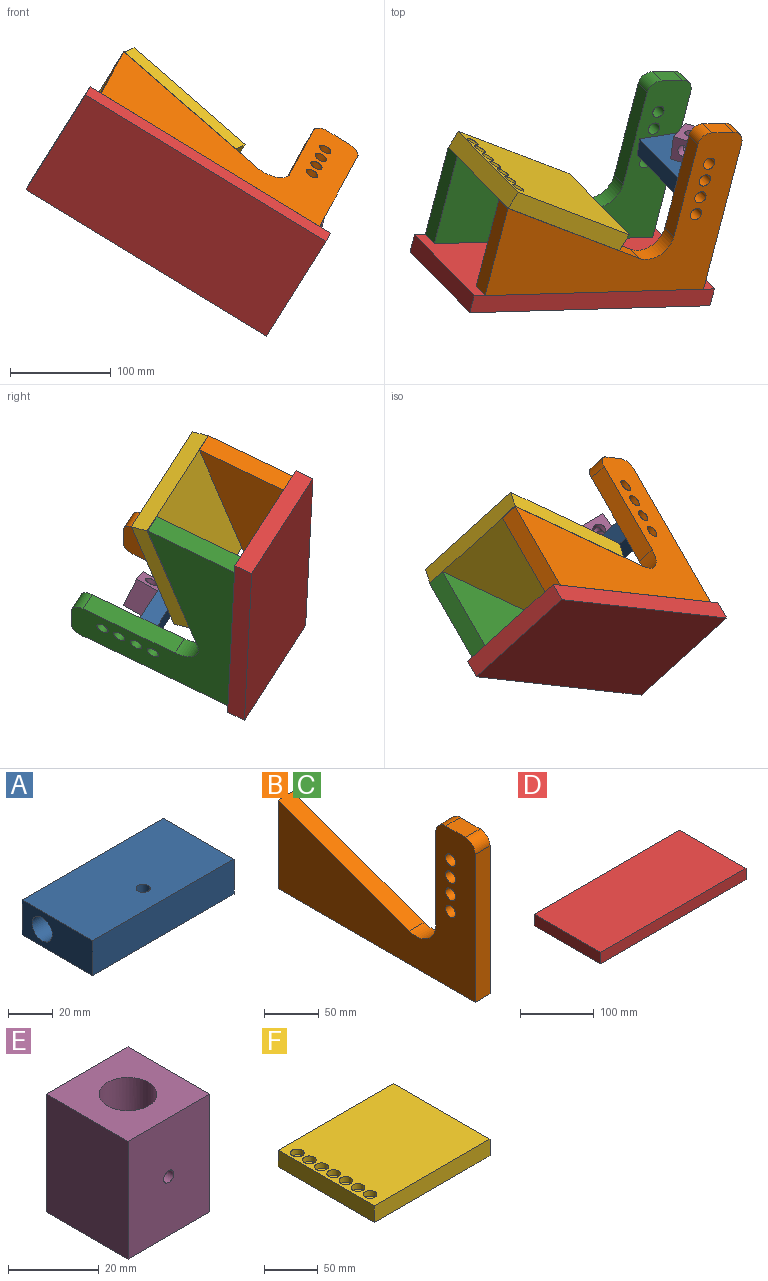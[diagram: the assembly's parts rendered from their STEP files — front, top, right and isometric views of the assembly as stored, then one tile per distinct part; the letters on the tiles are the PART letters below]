
ASSEMBLY  parts=6 mates=5
PART A: 8 faces, bbox 88.9x44.5x19.1 mm
  f0: plane 44.45x19.05mm, normal (-1,0,0), area 720.1mm2, adj f1,f3,f4,f5,f6
  f1: plane 88.9x19.05mm, normal (0,-1,0), area 1693.5mm2, adj f0,f2,f4,f5
  f2: plane 44.45x19.05mm, normal (1,0,0), area 720.1mm2, adj f1,f3,f4,f5,f6
  f3: plane 88.9x19.05mm, normal (0,1,0), area 1693.5mm2, adj f0,f2,f4,f5
  f4: plane 88.9x44.45mm, normal (0,0,1), area 3919.9mm2, adj f0,f1,f2,f3,f7
  f5: plane 88.9x44.45mm, normal (0,0,-1), area 3919.9mm2, adj f0,f1,f2,f3,f7
  f6: cylinder r=6.35mm len=88.9mm, axis (-1,0,0), area 3547mm2, adj f0,f2
  f7: cylinder r=3.17mm len=19.05mm, axis (0,0,1), area 380mm2, adj f4,f5
PART B: 15 faces, bbox 19.1x254x177.8 mm
  f0: plane 25.4x19.05mm, normal (0,0,1), area 483.9mm2, adj f1,f12,f13,f14
  f1: cylinder r=12.7mm len=19.05mm, axis (-1,0,0), area 380mm2, adj f0,f2,f13,f14
  f2: plane 165.1x19.05mm, normal (0,-1,0), area 3145.2mm2, adj f1,f3,f13,f14
  f3: plane 254x19.05mm, normal (0,0,-1), area 4838.7mm2, adj f2,f4,f13,f14
  f4: plane 98.8x19.05mm, normal (0,1,0), area 1882.1mm2, adj f3,f5,f13,f14
  f5: plane 169.11x61.55mm, normal (0,-0.34,0.94), area 3428.4mm2, adj f4,f6,f13,f14
  f6: cylinder r=25.4mm len=34.09mm, axis (-1,0,0), area 929mm2, adj f5,f7,f13,f14
  f7: plane 103.99x19.05mm, normal (0,1,0), area 1980.9mm2, adj f6,f12,f13,f14
  f8: cylinder r=6.35mm len=19.05mm, axis (-1,0,0), area 760.1mm2, adj f13,f14
  f9: cylinder r=6.35mm len=19.05mm, axis (-1,0,0), area 760.1mm2, adj f13,f14
  f10: cylinder r=6.35mm len=19.05mm, axis (-1,0,0), area 760.1mm2, adj f13,f14
  f11: cylinder r=6.35mm len=19.05mm, axis (-1,0,0), area 760.1mm2, adj f13,f14
  f12: cylinder r=12.7mm len=19.05mm, axis (-1,0,0), area 380mm2, adj f0,f7,f13,f14
  f13: plane 254x177.8mm, normal (1,0,0), area 21320mm2, adj f0,f1,f2,f3,f4,f5,f6,f7
  f14: plane 254x177.8mm, normal (-1,0,0), area 21320mm2, adj f0,f1,f2,f3,f4,f5,f6,f7
PART C: same geometry as B
PART D: 6 faces, bbox 279.4x127x19.1 mm
  f0: plane 127x19.05mm, normal (-1,0,0), area 2419.3mm2, adj f1,f3,f4,f5
  f1: plane 279.4x19.05mm, normal (0,-1,0), area 5322.6mm2, adj f0,f2,f4,f5
  f2: plane 127x19.05mm, normal (1,0,0), area 2419.3mm2, adj f1,f3,f4,f5
  f3: plane 279.4x19.05mm, normal (0,1,0), area 5322.6mm2, adj f0,f2,f4,f5
  f4: plane 279.4x127mm, normal (0,0,1), area 35483.8mm2, adj f0,f1,f2,f3
  f5: plane 279.4x127mm, normal (0,0,-1), area 35483.8mm2, adj f0,f1,f2,f3
PART E: 13 faces, bbox 25.4x25.4x31.8 mm
  f0: cylinder r=6.35mm len=15.88mm, axis (0,0,1), area 472.1mm2, adj f6,f8,f9,f10
  f1: plane 31.75x25.4mm, normal (-1,0,0), area 806.5mm2, adj f2,f4,f5,f6
  f2: plane 31.75x25.4mm, normal (0,-1,0), area 798.5mm2, adj f1,f3,f5,f6,f12
  f3: plane 31.75x25.4mm, normal (1,0,0), area 806.5mm2, adj f2,f4,f5,f6
  f4: plane 31.75x25.4mm, normal (0,1,0), area 679.8mm2, adj f1,f3,f5,f6,f8
  f5: plane 25.4x25.4mm, normal (0,0,1), area 518.5mm2, adj f1,f2,f3,f4,f7
  f6: plane 25.4x25.4mm, normal (0,0,-1), area 518.5mm2, adj f0,f1,f2,f3,f4
  f7: cylinder r=6.35mm len=15.88mm, axis (0,0,1), area 472.1mm2, adj f5,f8,f9,f10
  f8: cylinder r=6.35mm len=12.7mm, axis (0,1,0), area 345.4mm2, adj f0,f4,f7
  f9: cylinder r=6.35mm len=12.7mm, axis (0,1,0), area 46mm2, adj f0,f7,f11
  f10: cylinder r=6.35mm len=12.7mm, axis (0,1,0), area 46mm2, adj f0,f7,f11
  f11: plane 12.7x12.7mm, normal (0,1,0), area 118.8mm2, adj f9,f10,f12
  f12: cylinder r=1.59mm len=6.35mm, axis (0,-1,0), area 63.3mm2, adj f2,f11
PART F: 20 faces, bbox 152.4x127x19.1 mm
  f0: plane 152.4x19.05mm, normal (0,1,0), area 2903.2mm2, adj f1,f3,f4,f5
  f1: plane 127x19.05mm, normal (-1,0,0), area 2419.3mm2, adj f0,f2,f4,f5
  f2: plane 152.4x19.05mm, normal (0,-1,0), area 2903.2mm2, adj f1,f3,f4,f5
  f3: plane 127x19.05mm, normal (1,0,0), area 2419.3mm2, adj f0,f2,f4,f5
  f4: plane 152.4x127mm, normal (0,0,1), area 18468.1mm2, adj f0,f1,f2,f3,f6,f8,f10,f12
  f5: plane 152.4x127mm, normal (0,0,-1), area 19354.8mm2, adj f0,f1,f2,f3
  f6: cylinder r=6.35mm len=12.7mm, axis (0,0,1), area 253.4mm2, adj f4,f7
  f7: plane 12.7x12.7mm, normal (0,0,1), area 126.7mm2, adj f6
  f8: cylinder r=6.35mm len=12.7mm, axis (0,0,1), area 253.4mm2, adj f4,f9
  f9: plane 12.7x12.7mm, normal (0,0,1), area 126.7mm2, adj f8
  f10: cylinder r=6.35mm len=12.7mm, axis (0,0,1), area 253.4mm2, adj f4,f11
  f11: plane 12.7x12.7mm, normal (0,0,1), area 126.7mm2, adj f10
  f12: cylinder r=6.35mm len=12.7mm, axis (0,0,1), area 253.4mm2, adj f4,f13
  f13: plane 12.7x12.7mm, normal (0,0,1), area 126.7mm2, adj f12
  f14: cylinder r=6.35mm len=12.7mm, axis (0,0,1), area 253.4mm2, adj f4,f15
  f15: plane 12.7x12.7mm, normal (0,0,1), area 126.7mm2, adj f14
  f16: cylinder r=6.35mm len=12.7mm, axis (0,0,1), area 253.4mm2, adj f4,f17
  f17: plane 12.7x12.7mm, normal (0,0,1), area 126.7mm2, adj f16
  f18: cylinder r=6.35mm len=12.7mm, axis (0,0,1), area 253.4mm2, adj f4,f19
  f19: plane 12.7x12.7mm, normal (0,0,1), area 126.7mm2, adj f18
PLACE A rot(axis=(0.81,-0.53,0.25),125.6deg) t=(31.21,-91.95,6.23)mm
PLACE B rot(axis=(-0.21,0.58,0.79),122.4deg) t=(55.8,-247.6,35.79)mm
PLACE C rot(axis=(-0.21,0.58,0.79),122.4deg) t=(5.36,-195.94,-44.46)mm
PLACE D rot(axis=(-0.87,0.4,0.27),67.9deg) t=(-176.29,-271.24,166.43)mm fixed
PLACE E rot(axis=(0.1,0.96,0.24),160.1deg) t=(46.54,-125.19,61.77)mm
PLACE F rot(axis=(-0.81,0.58,0.1),77.9deg) t=(-112.54,-158.24,113.69)mm
MATE fastened D.f4 <-> C.f3  axis (0.23,0.88,0.42) through (-111.97,-190.12,7.4)mm
MATE fastened F.f5 <-> B.f5  axis (-0.51,-0.83,-0.22) through (-112.54,-158.24,113.69)mm
MATE revolute E.f8 <-> A.f7  axis (-0.11,-0.87,-0.49) through (40.84,-115.06,45.09)mm
MATE revolute A.f6 <-> B.f10  axis (0.47,-0.48,0.74) through (43.84,-147.34,82.22)mm
MATE fastened B.f3 <-> D.f4  axis (-0.23,-0.88,-0.42) through (-57.09,-246.33,94.74)mm
